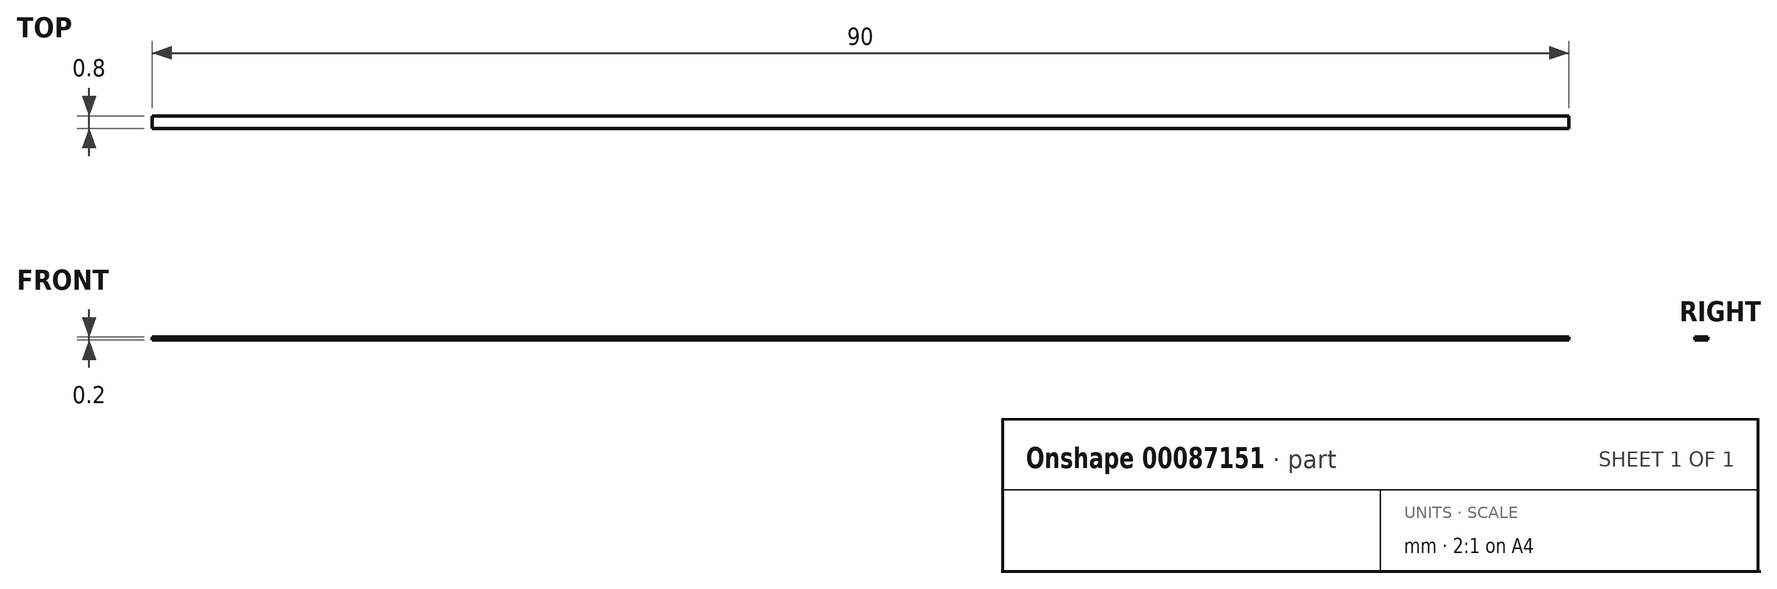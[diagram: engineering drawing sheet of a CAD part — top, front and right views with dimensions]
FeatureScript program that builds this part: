
annotation { "Feature Type Name" : "Feature", "Feature Type Description" : "" }
export const myFeature = defineFeature(function(context is Context, id is Id, definition is map)
    precondition{}
    {
        {
            var Q0;
            Q0=qCreatedBy(makeId("Top.planeOp"),FACE);
            var sketch = newSketch(context, id + "F0", { "sketchPlane" : qUnion([Q0])});
            skLineSegment(sketch, "E0.bottom", {"start": v(0.4, 45) * mm, "end": v(-0.4, 45) * mm});
            skLineSegment(sketch, "E0.top", {"start": v(0.4, -45) * mm, "end": v(-0.4, -45) * mm});
            skLineSegment(sketch, "E0.left", {"start": v(0.4, 45) * mm, "end": v(0.4, -45) * mm});
            skLineSegment(sketch, "E0.right", {"start": v(-0.4, 45) * mm, "end": v(-0.4, -45) * mm});
            skPoint(sketch, "E0.middle", {"position": v(0, 0) * mm});
            skSolve(sketch);
        }
        {
            var Q0;
            Q0 = qSketchRegion(id + "F0", true);
            extrude(context, id + "F1", {"entities" : qUnion([Q0]), "endBound" : BoundingType.SYMMETRIC, "depth" : 0.2 * mm});
        }
        {
            var Q0;
            Q0=qCreatedBy(makeId("Front.planeOp"),FACE);
            var sketch = newSketch(context, id + "F2", { "sketchPlane" : qUnion([Q0])});
            skLineSegment(sketch, "E1", {"start": v(0, 0) * mm, "end": v(0, 44.04) * mm});
            skSolve(sketch);
        }
        {
            var Q0;
            Q0=makeQuery(id+"F1.opExtrude","SWEPT_BODY",BODY,{"disambiguationData":[OSD([sQuery(id+"F0.wireOp",EDGE,"E0.bottom"),sQuery(id+"F0.wireOp",EDGE,"E0.top"),sQuery(id+"F0.wireOp",EDGE,"E0.left"),sQuery(id+"F0.wireOp",EDGE,"E0.right")])]});
            var Q1;
            Q1=sQuery(id+"F2.wireOp",EDGE,"E1");
            transform(context, id + "F3", {"entities" : qUnion([Q0]), "transformType" : TransformType.ROTATION, "transformAxis" : qUnion([Q1]), "angle" : 90 * degree, "makeCopy" : false});
        }
    });
